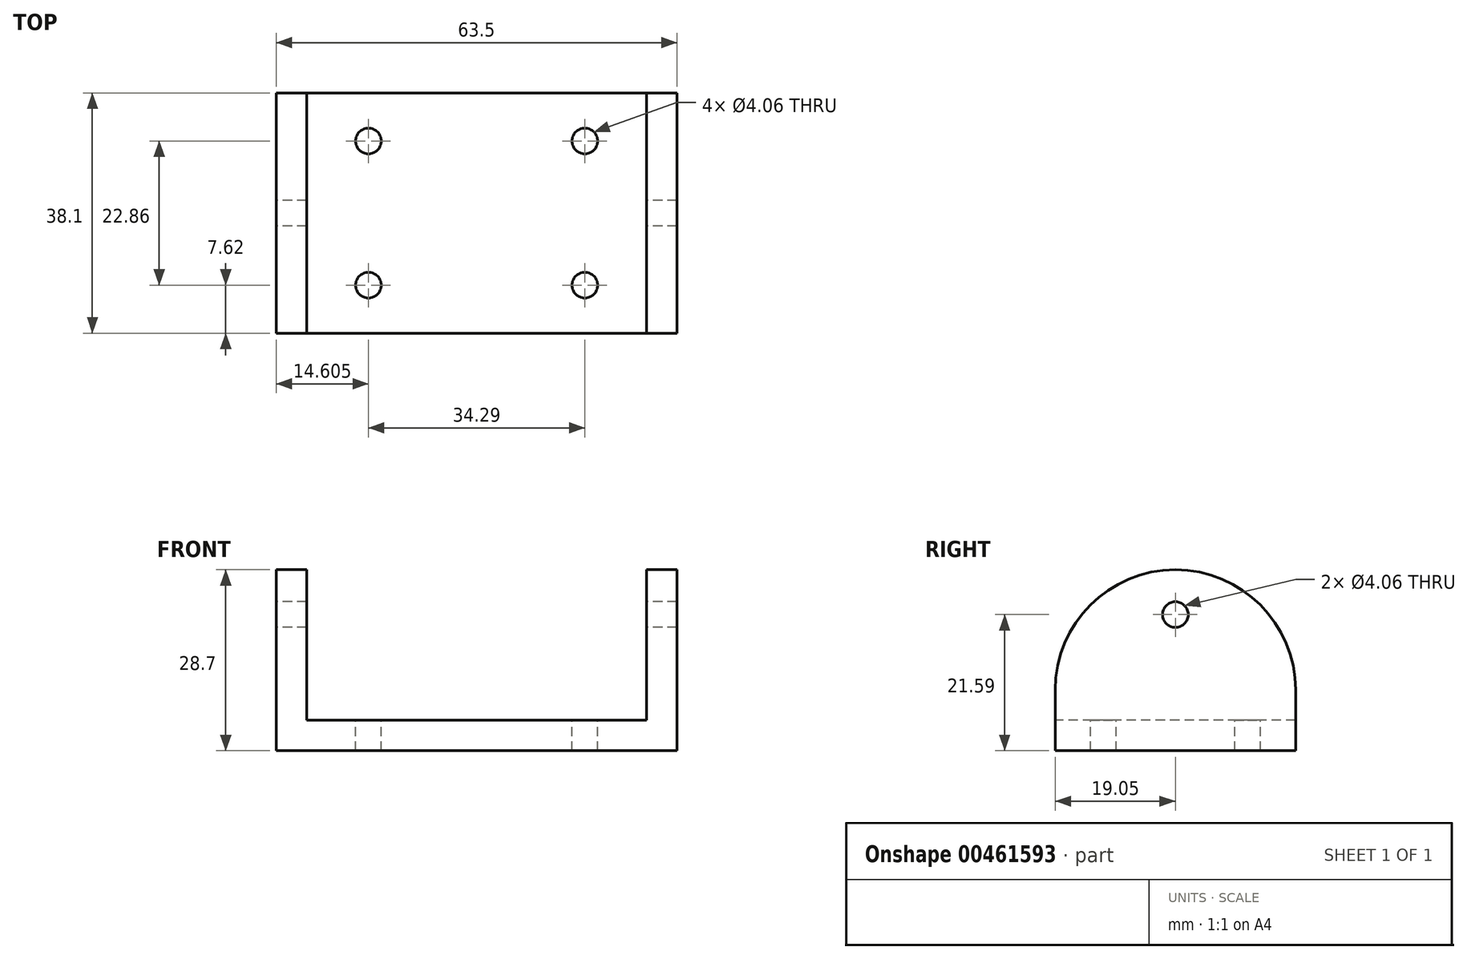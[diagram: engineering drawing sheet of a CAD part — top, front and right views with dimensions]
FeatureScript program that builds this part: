
annotation { "Feature Type Name" : "Feature", "Feature Type Description" : "" }
export const myFeature = defineFeature(function(context is Context, id is Id, definition is map)
    precondition{}
    {
        {
            var Q0;
            Q0=qCreatedBy(makeId("Right.planeOp"),FACE);
            var sketch = newSketch(context, id + "F0", { "sketchPlane" : qUnion([Q0])});
            skLineSegment(sketch, "E0", {"start": v(-19.05, 9.65) * mm, "end": v(-19.05, 0) * mm});
            skLineSegment(sketch, "E1", {"start": v(-19.05, 0) * mm, "end": v(19.05, 0) * mm});
            skLineSegment(sketch, "E2", {"start": v(19.05, 0) * mm, "end": v(19.05, 9.65) * mm});
            skArc(sketch, "E3", {"start": v(19.05, 9.65) * mm, "mid": v(0, 28.7) * mm, "end": v(-19.05, 9.65) * mm});
            skCircle(sketch, "E4", {"center": v(0, 21.59) * mm, "radius": 2.03 * mm});
            skPoint(sketch, "E5", {"position": v(0, 28.7) * mm});
            skSolve(sketch);
        }
        {
            var Q0;
            Q0 = qSketchRegion(id + "F0", true);
            extrude(context, id + "F1", {"entities" : qUnion([Q0]), "depth" : 63.5 * mm});
        }
        {
            var Q0;
            Q0=makeQuery(id+"F1.opExtrude","SWEPT_FACE",FACE,{"disambiguationData":[OSD([sQuery(id+"F0.wireOp",EDGE,"E0")])]});
            var sketch = newSketch(context, id + "F2", { "sketchPlane" : qUnion([Q0])});
            skLineSegment(sketch, "E6.bottom", {"start": v(4.83, 4.83) * mm, "end": v(58.67, 4.83) * mm});
            skLineSegment(sketch, "E6.top", {"start": v(4.83, 28.7) * mm, "end": v(58.67, 28.7) * mm});
            skLineSegment(sketch, "E6.left", {"start": v(4.83, 4.83) * mm, "end": v(4.83, 28.7) * mm});
            skLineSegment(sketch, "E6.right", {"start": v(58.67, 4.83) * mm, "end": v(58.67, 28.7) * mm});
            skPoint(sketch, "E7", {"position": v(31.75, 0) * mm});
            skPoint(sketch, "E8", {"position": v(31.75, 4.83) * mm});
            skPoint(sketch, "E9", {"position": v(63.5, 4.83) * mm});
            skLineSegment(sketch, "E10", {"start": v(4.83, 4.83) * mm, "end": v(4.83, 0) * mm, "construction": true});
            skLineSegment(sketch, "E11", {"start": v(4.83, 4.83) * mm, "end": v(0, 4.83) * mm, "construction": true});
            skSolve(sketch);
        }
        {
            var Q0;
            Q0 = qSketchRegion(id + "F2", true);
            var Q1;
            Q1=makeQuery(id+"F1.opExtrude","SWEPT_BODY",BODY,{"disambiguationData":[OSD([sQuery(id+"F0.wireOp",EDGE,"E0"),sQuery(id+"F0.wireOp",EDGE,"E1"),sQuery(id+"F0.wireOp",EDGE,"E2"),sQuery(id+"F0.wireOp",EDGE,"E3"),sQuery(id+"F0.wireOp",EDGE,"E4")])]});
            extrude(context, id + "F3", {"entities" : qUnion([Q0]), "operationType" : NewBodyOperationType.REMOVE, "endBound" : BoundingType.UP_TO_BODY, "oppositeDirection" : true, "endBoundEntityBody" : qUnion([Q1]), "depth" : 25.4 * mm});
        }
        {
            var Q0;
            Q0=makeQuery(id+"F3.boolean.opBoolean","COPY",FACE,{"derivedFrom":makeQuery(id+"F3.opExtrude","SWEPT_FACE",FACE,{"disambiguationData":[OSD([sQuery(id+"F2.wireOp",EDGE,"E6.bottom")])]})});
            var sketch = newSketch(context, id + "F4", { "sketchPlane" : qUnion([Q0])});
            skLineSegment(sketch, "E12", {"start": v(4.83, 0) * mm, "end": v(58.67, 0) * mm, "construction": true});
            skPoint(sketch, "E13", {"position": v(31.75, 0) * mm});
            skLineSegment(sketch, "E14.bottom", {"start": v(14.6, 11.43) * mm, "end": v(48.9, 11.43) * mm, "construction": true});
            skLineSegment(sketch, "E14.top", {"start": v(14.6, -11.43) * mm, "end": v(48.9, -11.43) * mm, "construction": true});
            skLineSegment(sketch, "E14.left", {"start": v(14.6, 11.43) * mm, "end": v(14.6, -11.43) * mm, "construction": true});
            skLineSegment(sketch, "E14.right", {"start": v(48.9, 11.43) * mm, "end": v(48.9, -11.43) * mm, "construction": true});
            skCircle(sketch, "E15", {"center": v(14.6, 11.43) * mm, "radius": 2.03 * mm});
            skCircle(sketch, "E16", {"center": v(14.6, -11.43) * mm, "radius": 2.03 * mm});
            skCircle(sketch, "E17", {"center": v(48.9, -11.43) * mm, "radius": 2.03 * mm});
            skCircle(sketch, "E18", {"center": v(48.9, 11.43) * mm, "radius": 2.03 * mm});
            skSolve(sketch);
        }
        {
            var Q0;
            Q0 = qSketchRegion(id + "F4", true);
            var Q1;
            Q1=makeQuery(id+"F1.opExtrude","SWEPT_FACE",FACE,{"disambiguationData":[OSD([sQuery(id+"F0.wireOp",EDGE,"E1")])]});
            extrude(context, id + "F5", {"entities" : qUnion([Q0]), "operationType" : NewBodyOperationType.REMOVE, "endBound" : BoundingType.UP_TO_SURFACE, "oppositeDirection" : true, "endBoundEntityFace" : qUnion([Q1]), "depth" : 25.4 * mm});
        }
    });
